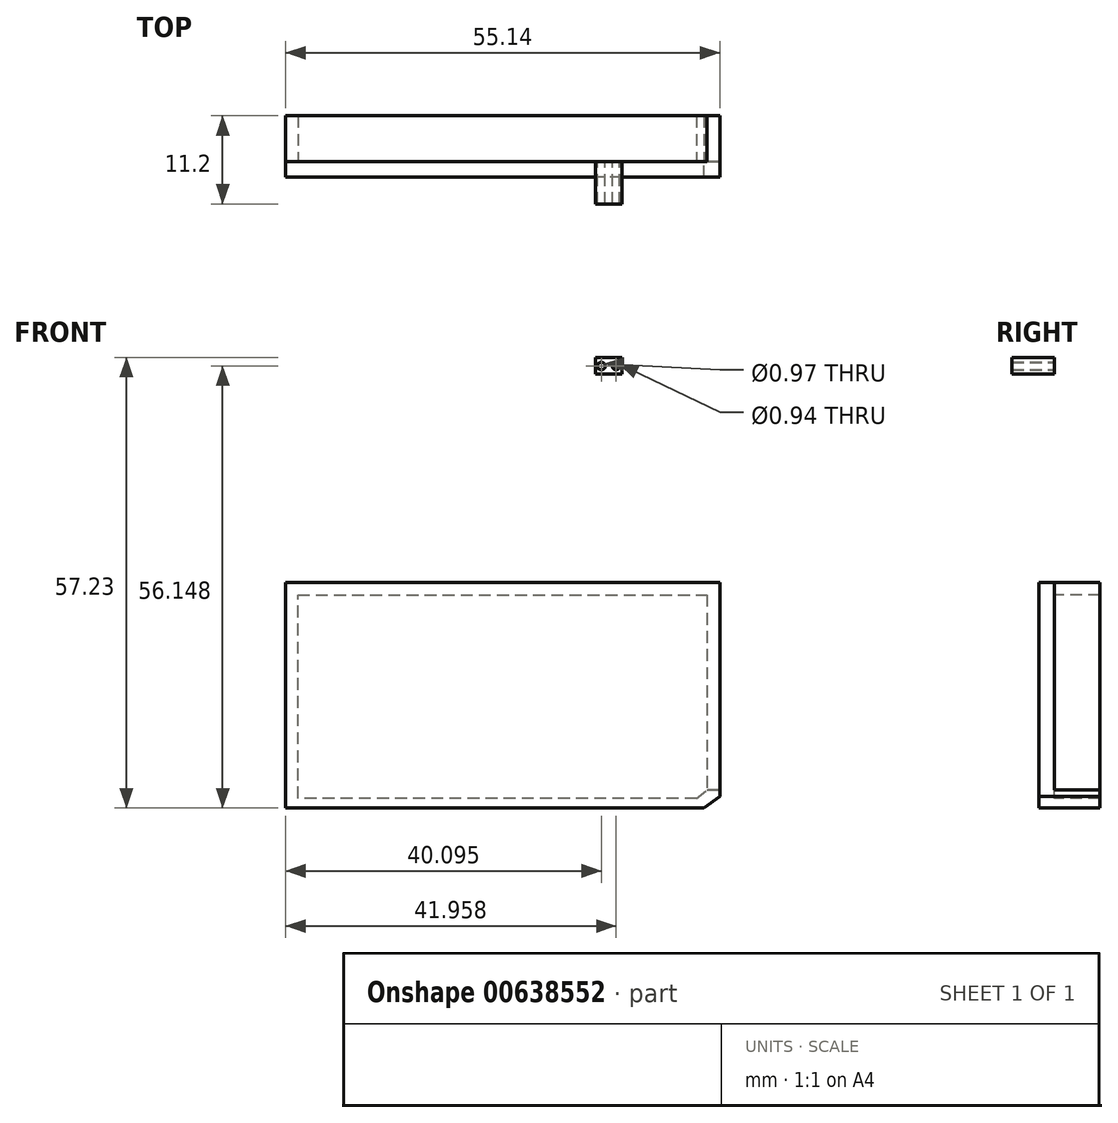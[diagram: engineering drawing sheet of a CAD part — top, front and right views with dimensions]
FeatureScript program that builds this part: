
annotation { "Feature Type Name" : "Feature", "Feature Type Description" : "" }
export const myFeature = defineFeature(function(context is Context, id is Id, definition is map)
    precondition{}
    {
        {
            var Q0;
            Q0=qCreatedBy(makeId("Front.planeOp"),FACE);
            var sketch = newSketch(context, id + "F0", { "sketchPlane" : qUnion([Q0])});
            skLineSegment(sketch, "E0.MirrorCS", {"start": v(66.07, 11.34) * mm, "end": v(10.94, 11.34) * mm});
            skLineSegment(sketch, "E1.MirrorCS", {"start": v(10.94, 11.34) * mm, "end": v(10.94, -15.17) * mm});
            skLineSegment(sketch, "E2.MirrorCS", {"start": v(10.94, -15.17) * mm, "end": v(10.94, -17.32) * mm});
            skLineSegment(sketch, "E3.MirrorCS", {"start": v(10.94, -17.32) * mm, "end": v(13.2, -17.32) * mm});
            skLineSegment(sketch, "E4.MirrorCS", {"start": v(13.2, -17.32) * mm, "end": v(64.08, -17.32) * mm});
            skLineSegment(sketch, "E5.MirrorCS", {"start": v(64.08, -17.32) * mm, "end": v(66.07, -15.83) * mm});
            skLineSegment(sketch, "E6.MirrorCS", {"start": v(66.07, -15.83) * mm, "end": v(66.07, 11.34) * mm});
            skSolve(sketch);
        }
        {
            var Q0;
            Q0=makeQuery(id+"F0.imprint","IMPRINT",FACE,{"disambiguationData":[TD([[makeQuery(id+"F0.imprint","IMPRINT",EDGE,{"derivedFrom":sQuery(id+"F0.wireOp",EDGE,"E0.MirrorCS")}),1.0]])]});
            extrude(context, id + "F1", {"entities" : qUnion([Q0]), "depth" : 2 * mm, "offsetDistance" : 25 * mm});
        }
        {
            var Q0;
            Q0=qCreatedBy(makeId("Front.planeOp"),FACE);
            var sketch = newSketch(context, id + "F2", { "sketchPlane" : qUnion([Q0])});
            skLineSegment(sketch, "E7.bottom", {"start": v(65.78, 11.48) * mm, "end": v(64.47, 11.48) * mm});
            skLineSegment(sketch, "E7.top", {"start": v(65.78, -15.02) * mm, "end": v(64.47, -15.02) * mm});
            skLineSegment(sketch, "E7.left", {"start": v(65.78, 11.48) * mm, "end": v(65.78, -15.02) * mm});
            skLineSegment(sketch, "E7.right", {"start": v(64.47, 11.48) * mm, "end": v(64.47, -15.02) * mm});
            skSolve(sketch);
        }
        {
            var Q0;
            Q0 = qSketchRegion(id + "F2", true);
            extrude(context, id + "F3", {"entities" : qUnion([Q0]), "operationType" : NewBodyOperationType.ADD, "oppositeDirection" : true, "depth" : 5.8 * mm, "offsetDistance" : 25 * mm});
        }
        {
            var Q0;
            Q0=makeQuery(id+"F3.opExtrude","SWEPT_FACE",FACE,{"disambiguationData":[OSD([sQuery(id+"F2.wireOp",EDGE,"E7.left")])]});
            extrude(context, id + "F4", {"entities" : qUnion([Q0]), "operationType" : NewBodyOperationType.ADD, "depth" : 0.3 * mm, "offsetDistance" : 25 * mm});
        }
        {
            var Q0;
            Q0=qCreatedBy(makeId("Front.planeOp"),FACE);
            var sketch = newSketch(context, id + "F5", { "sketchPlane" : qUnion([Q0])});
            skLineSegment(sketch, "E8", {"start": v(63.13, -16.1) * mm, "end": v(12.48, -16.1) * mm});
            skLineSegment(sketch, "E9", {"start": v(12.48, -16.1) * mm, "end": v(12.48, 9.76) * mm});
            skLineSegment(sketch, "E10", {"start": v(12.48, 9.76) * mm, "end": v(64.38, 9.76) * mm});
            skLineSegment(sketch, "E11", {"start": v(64.38, 9.76) * mm, "end": v(64.38, 11.32) * mm});
            skLineSegment(sketch, "E12", {"start": v(64.38, 11.32) * mm, "end": v(10.94, 11.32) * mm});
            skLineSegment(sketch, "E13", {"start": v(10.94, 11.32) * mm, "end": v(10.94, -17.32) * mm});
            skLineSegment(sketch, "E14", {"start": v(10.94, -17.32) * mm, "end": v(64.08, -17.32) * mm});
            skLineSegment(sketch, "E15", {"start": v(64.08, -17.32) * mm, "end": v(66.07, -15.84) * mm});
            skLineSegment(sketch, "E16", {"start": v(66.07, -15.84) * mm, "end": v(66.07, -15.02) * mm});
            skLineSegment(sketch, "E17", {"start": v(63.13, -16.1) * mm, "end": v(64.47, -15.02) * mm});
            skLineSegment(sketch, "E18", {"start": v(64.47, -15.02) * mm, "end": v(66.07, -15.02) * mm});
            skSolve(sketch);
        }
        {
            var Q0;
            Q0=makeQuery(id+"F5.imprint","IMPRINT",FACE,{"disambiguationData":[TD([[makeQuery(id+"F5.imprint","IMPRINT",EDGE,{"derivedFrom":sQuery(id+"F5.wireOp",EDGE,"E8")}),1.0]])]});
            extrude(context, id + "F6", {"entities" : qUnion([Q0]), "operationType" : NewBodyOperationType.ADD, "oppositeDirection" : true, "depth" : 5.8 * mm, "offsetDistance" : 25 * mm});
        }
        {
            var Q0;
            {var subQ0=sQuery(id+"F2.wireOp",EDGE,"E7.bottom");Q0=makeQuery(id+"F4.boolean.opBoolean","MERGE",FACE,{"derivedFrom":[makeQuery(id+"F3.opExtrude","SWEPT_FACE",FACE,{"disambiguationData":[OSD([subQ0])]}),makeQuery(id+"F4.opExtrude","SWEPT_FACE",FACE,{"disambiguationData":[OSD([subQ0,sQuery(id+"F2.wireOp",EDGE,"E7.left")])]})]});}
            extrude(context, id + "F7", {"entities" : qUnion([Q0]), "operationType" : NewBodyOperationType.REMOVE, "oppositeDirection" : true, "depth" : 0.14 * mm, "offsetDistance" : 25 * mm});
        }
        {
            var Q0;
            Q0=makeQuery(id+"F6.opExtrude","SWEPT_FACE",FACE,{"disambiguationData":[OSD([sQuery(id+"F5.wireOp",EDGE,"E11")])]});
            extrude(context, id + "F8", {"entities" : qUnion([Q0]), "operationType" : NewBodyOperationType.ADD, "depth" : 0.13 * mm, "offsetDistance" : 25 * mm});
        }
        {
            var Q0;
            Q0=qCreatedBy(makeId("Front.planeOp"),FACE);
            var sketch = newSketch(context, id + "F9", { "sketchPlane" : qUnion([Q0])});
            skLineSegment(sketch, "E19.bottom", {"start": v(11.1, 17.86) * mm, "end": v(65.64, 17.86) * mm});
            skLineSegment(sketch, "E19.top", {"start": v(11.1, 47.52) * mm, "end": v(65.64, 47.52) * mm});
            skLineSegment(sketch, "E19.left", {"start": v(11.1, 17.86) * mm, "end": v(11.1, 47.52) * mm});
            skLineSegment(sketch, "E19.right", {"start": v(65.64, 17.86) * mm, "end": v(65.64, 47.52) * mm});
            skLineSegment(sketch, "E20.bottom", {"start": v(50.29, 39.91) * mm, "end": v(53.63, 39.91) * mm});
            skLineSegment(sketch, "E20.top", {"start": v(50.29, 37.83) * mm, "end": v(53.63, 37.83) * mm});
            skLineSegment(sketch, "E20.left", {"start": v(50.29, 39.91) * mm, "end": v(50.29, 37.83) * mm});
            skLineSegment(sketch, "E20.right", {"start": v(53.63, 39.91) * mm, "end": v(53.63, 37.83) * mm});
            skCircle(sketch, "E21", {"center": v(51.04, 38.83) * mm, "radius": 0.49 * mm});
            skCircle(sketch, "E22", {"center": v(52.9, 38.83) * mm, "radius": 0.47 * mm});
            skSolve(sketch);
        }
        {
            var Q0;
            Q0=makeQuery(id+"F9.imprint","IMPRINT",FACE,{"disambiguationData":[TD([[makeQuery(id+"F9.imprint","IMPRINT",EDGE,{"derivedFrom":sQuery(id+"F9.wireOp",EDGE,"E20.bottom")}),-1.0]])]});
            extrude(context, id + "F10", {"entities" : qUnion([Q0]), "operationType" : NewBodyOperationType.ADD, "depth" : 5.4 * mm, "offsetDistance" : 25 * mm});
        }
    });
